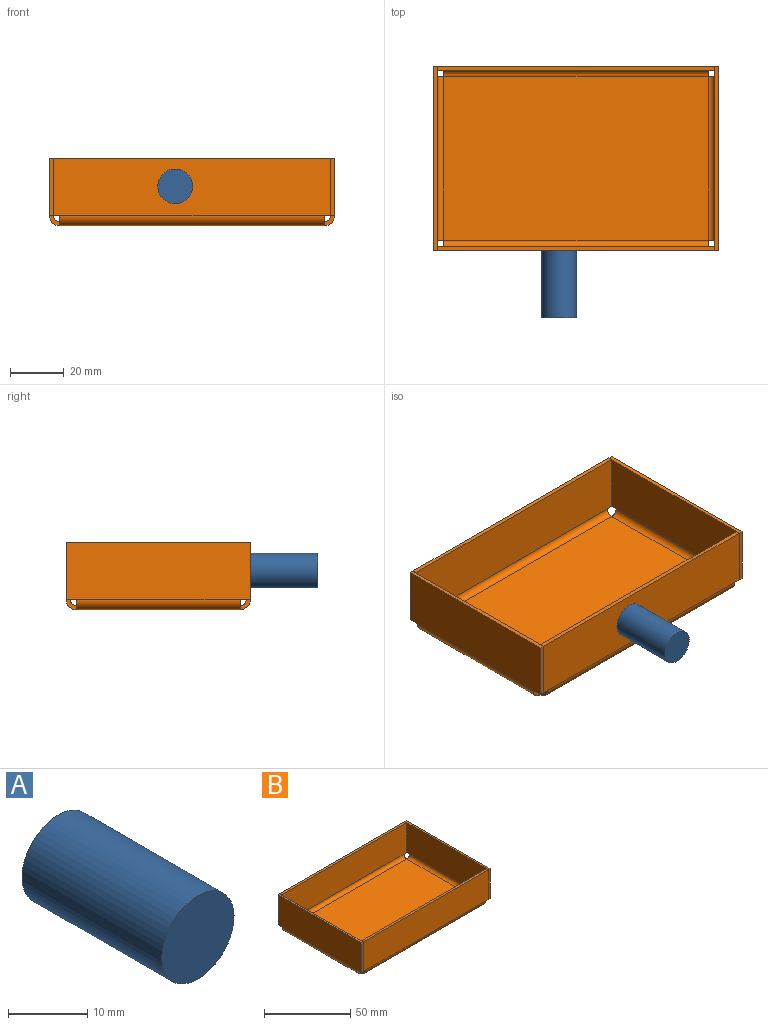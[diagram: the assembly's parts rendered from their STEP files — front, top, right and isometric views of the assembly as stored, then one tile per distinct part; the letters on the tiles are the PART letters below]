
ASSEMBLY  parts=2 mates=1
PART A: 3 faces, bbox 12.9x25x12.9 mm
  f0: cylinder r=6.45mm len=25mm, axis (0,1,0), area 1013mm2, adj f1,f2
  f1: plane 12.9x12.9mm, normal (0,-1,0), area 130.6mm2, adj f0
  f2: plane 12.9x12.9mm, normal (0,1,0), area 130.6mm2, adj f0
PART B: 46 faces, bbox 105.8x68.3x25 mm
  f0: plane 98.18x60.71mm, normal (0,0,-1), area 5960.8mm2, adj f11,f22,f33,f44
  f1: plane 98.18x60.71mm, normal (0,0,1), area 5960.8mm2, adj f12,f23,f34,f45
  f2: plane 3.8x1.5mm, normal (0,0,-1), area 5.7mm2, adj f4,f7,f8,f9
  f3: plane 68.31x1.5mm, normal (0,0,1), area 102.5mm2, adj f4,f6,f7,f8
  f4: plane 21.2x1.5mm, normal (0,1,0), area 31.8mm2, adj f2,f3,f7,f8
  f5: plane 3.8x1.5mm, normal (0,0,-1), area 5.7mm2, adj f6,f7,f8,f10
  f6: plane 21.2x1.5mm, normal (0,-1,0), area 31.8mm2, adj f3,f5,f7,f8
  f7: plane 68.31x21.2mm, normal (-1,0,0), area 1448.3mm2, adj f2,f3,f4,f5,f6,f11
  f8: plane 68.31x21.2mm, normal (1,0,0), area 1448.3mm2, adj f2,f3,f4,f5,f6,f12
  f9: plane 3.8x3.8mm, normal (0,1,0), area 7.2mm2, adj f2,f11,f12,f31
  f10: plane 3.8x3.8mm, normal (0,-1,0), area 7.2mm2, adj f5,f11,f12,f42
  f11: cylinder r=3.8mm len=60.71mm, axis (0,1,0), area 362.4mm2, adj f0,f7,f9,f10
  f12: cylinder r=2.3mm len=60.71mm, axis (0,1,0), area 219.4mm2, adj f1,f8,f9,f10
  f13: plane 3.8x1.5mm, normal (0,0,-1), area 5.7mm2, adj f15,f18,f19,f21
  f14: plane 68.31x1.5mm, normal (0,0,1), area 102.5mm2, adj f15,f17,f18,f19
  f15: plane 21.2x1.5mm, normal (0,-1,0), area 31.8mm2, adj f13,f14,f18,f19
  f16: plane 3.8x1.5mm, normal (0,0,-1), area 5.7mm2, adj f17,f18,f19,f20
  f17: plane 21.2x1.5mm, normal (0,1,0), area 31.8mm2, adj f14,f16,f18,f19
  f18: plane 68.31x21.2mm, normal (1,0,0), area 1448.3mm2, adj f13,f14,f15,f16,f17,f22
  f19: plane 68.31x21.2mm, normal (-1,0,0), area 1448.3mm2, adj f13,f14,f15,f16,f17,f23
  f20: plane 3.8x3.8mm, normal (0,1,0), area 7.2mm2, adj f16,f22,f23,f32
  f21: plane 3.8x3.8mm, normal (0,-1,0), area 7.2mm2, adj f13,f22,f23,f43
  f22: cylinder r=3.8mm len=60.71mm, axis (0,1,0), area 362.4mm2, adj f0,f18,f20,f21
  f23: cylinder r=2.3mm len=60.71mm, axis (0,1,0), area 219.4mm2, adj f1,f19,f20,f21
  f24: plane 2.28x1.5mm, normal (0,0,-1), area 3.4mm2, adj f26,f29,f30,f32
  f25: plane 102.74x1.5mm, normal (0,0,1), area 154.1mm2, adj f26,f28,f29,f30
  f26: plane 21.2x1.5mm, normal (1,0,0), area 31.8mm2, adj f24,f25,f29,f30
  f27: plane 2.28x1.5mm, normal (0,0,-1), area 3.4mm2, adj f28,f29,f30,f31
  f28: plane 21.2x1.5mm, normal (-1,0,0), area 31.8mm2, adj f25,f27,f29,f30
  f29: plane 102.74x21.2mm, normal (0,1,0), area 2178mm2, adj f24,f25,f26,f27,f28,f33
  f30: plane 102.74x21.2mm, normal (0,-1,0), area 2178mm2, adj f24,f25,f26,f27,f28,f34
  f31: plane 3.8x3.8mm, normal (-1,0,0), area 7.2mm2, adj f9,f27,f33,f34
  f32: plane 3.8x3.8mm, normal (1,0,0), area 7.2mm2, adj f20,f24,f33,f34
  f33: cylinder r=3.8mm len=98.18mm, axis (-1,0,0), area 586mm2, adj f0,f29,f31,f32
  f34: cylinder r=2.3mm len=98.18mm, axis (-1,0,0), area 354.7mm2, adj f1,f30,f31,f32
  f35: plane 2.28x1.5mm, normal (0,0,-1), area 3.4mm2, adj f37,f40,f41,f42
  f36: plane 102.74x1.5mm, normal (0,0,1), area 154.1mm2, adj f37,f39,f40,f41
  f37: plane 21.2x1.5mm, normal (-1,0,0), area 31.8mm2, adj f35,f36,f40,f41
  f38: plane 2.28x1.5mm, normal (0,0,-1), area 3.4mm2, adj f39,f40,f41,f43
  f39: plane 21.2x1.5mm, normal (1,0,0), area 31.8mm2, adj f36,f38,f40,f41
  f40: plane 102.74x21.2mm, normal (0,-1,0), area 2178mm2, adj f35,f36,f37,f38,f39,f44
  f41: plane 102.74x21.2mm, normal (0,1,0), area 2178mm2, adj f35,f36,f37,f38,f39,f45
  f42: plane 3.8x3.8mm, normal (-1,0,0), area 7.2mm2, adj f10,f35,f44,f45
  f43: plane 3.8x3.8mm, normal (1,0,0), area 7.2mm2, adj f21,f38,f44,f45
  f44: cylinder r=3.8mm len=98.18mm, axis (-1,0,0), area 586mm2, adj f0,f40,f42,f43
  f45: cylinder r=2.3mm len=98.18mm, axis (-1,0,0), area 354.7mm2, adj f1,f41,f42,f43
PLACE A t=(-163.71,-54.53,52.5)mm
PLACE B t=(-37.3,-53.03,34.22)mm
MATE planar A.f0 <-> B.f40  axis (0,1,0) through (-94.9,-54.53,48.78)mm
